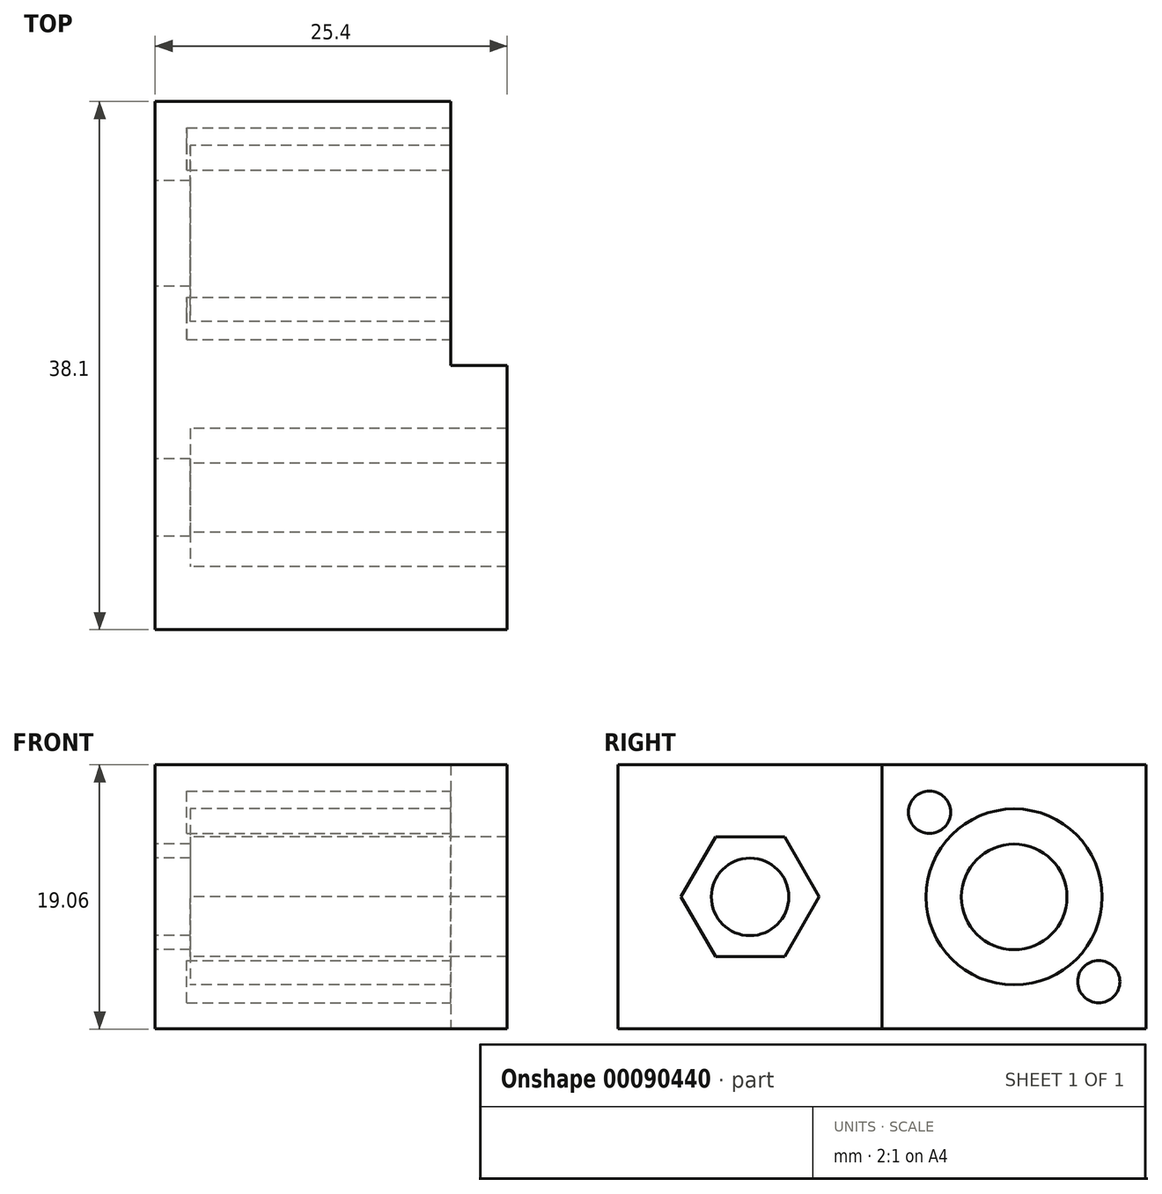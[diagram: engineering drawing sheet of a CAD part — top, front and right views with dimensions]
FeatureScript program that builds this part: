
annotation { "Feature Type Name" : "Feature", "Feature Type Description" : "" }
export const myFeature = defineFeature(function(context is Context, id is Id, definition is map)
    precondition{}
    {
        {
            var Q0;
            Q0=qCreatedBy(makeId("Right.planeOp"),FACE);
            var sketch = newSketch(context, id + "F0", { "sketchPlane" : qUnion([Q0])});
            skLineSegment(sketch, "E0", {"start": v(0, 0) * mm, "end": v(9.53, 0) * mm, "construction": true});
            skLineSegment(sketch, "E1", {"start": v(0, 0) * mm, "end": v(-9.53, 0) * mm, "construction": true});
            skLineSegment(sketch, "E2.bottom", {"start": v(-19.05, 9.53) * mm, "end": v(19.05, 9.52) * mm});
            skLineSegment(sketch, "E2.top", {"start": v(-19.05, -9.52) * mm, "end": v(19.05, -9.52) * mm});
            skLineSegment(sketch, "E2.left", {"start": v(-19.05, 9.53) * mm, "end": v(-19.05, -9.52) * mm});
            skLineSegment(sketch, "E2.right", {"start": v(19.05, 9.52) * mm, "end": v(19.05, -9.53) * mm});
            skPoint(sketch, "E2.middle", {"position": v(0, 0) * mm});
            skCircle(sketch, "E3.cCircle", {"center": v(-9.53, 0) * mm, "radius": 4.32 * mm, "construction": true});
            skLineSegment(sketch, "E3.0", {"start": v(-12.02, 4.32) * mm, "end": v(-7.03, 4.32) * mm});
            skLineSegment(sketch, "E3.1", {"start": v(-7.03, 4.32) * mm, "end": v(-4.54, 0) * mm});
            skLineSegment(sketch, "E3.2", {"start": v(-4.54, 0) * mm, "end": v(-7.03, -4.32) * mm});
            skLineSegment(sketch, "E3.3", {"start": v(-7.03, -4.32) * mm, "end": v(-12.02, -4.32) * mm});
            skLineSegment(sketch, "E3.4", {"start": v(-12.02, -4.32) * mm, "end": v(-14.51, 0) * mm});
            skLineSegment(sketch, "E3.5", {"start": v(-14.51, 0) * mm, "end": v(-12.02, 4.32) * mm});
            skPoint(sketch, "E3.0.midPoint", {"position": v(-9.53, 4.32) * mm});
            skCircle(sketch, "E4", {"center": v(9.53, 0) * mm, "radius": 6.35 * mm});
            skSolve(sketch);
        }
        {
            var Q0;
            Q0=makeQuery(id+"F0.imprint","IMPRINT",FACE,{"disambiguationData":[TD([[makeQuery(id+"F0.imprint","IMPRINT",EDGE,{"derivedFrom":sQuery(id+"F0.wireOp",EDGE,"E2.bottom")}),-1.0]])]});
            extrude(context, id + "F1", {"entities" : qUnion([Q0]), "depth" : 25.4 * mm});
        }
        {
            var Q0;
            Q0=makeQuery(id+"F1.opExtrude","CAP_FACE",FACE,{"disambiguationData":[OSD([sQuery(id+"F0.wireOp",EDGE,"E2.bottom"),sQuery(id+"F0.wireOp",EDGE,"E2.top"),sQuery(id+"F0.wireOp",EDGE,"E2.left"),sQuery(id+"F0.wireOp",EDGE,"E2.right"),sQuery(id+"F0.wireOp",EDGE,"E3.0"),sQuery(id+"F0.wireOp",EDGE,"E3.1"),sQuery(id+"F0.wireOp",EDGE,"E3.2"),sQuery(id+"F0.wireOp",EDGE,"E3.3"),sQuery(id+"F0.wireOp",EDGE,"E3.4"),sQuery(id+"F0.wireOp",EDGE,"E3.5"),sQuery(id+"F0.wireOp",EDGE,"E4")])],"isStart":true});
            var sketch = newSketch(context, id + "F2", { "sketchPlane" : qUnion([Q0])});
            skCircle(sketch, "E5", {"center": v(-9.53, 0) * mm, "radius": 3.81 * mm});
            skCircle(sketch, "E6", {"center": v(9.52, 0) * mm, "radius": 2.8 * mm});
            skLineSegment(sketch, "E7", {"start": v(12.02, 4.32) * mm, "end": v(7.03, -4.32) * mm, "construction": true});
            skLineSegment(sketch, "E8.bottom", {"start": v(-19.05, 9.52) * mm, "end": v(19.05, 9.52) * mm});
            skLineSegment(sketch, "E8.top", {"start": v(-19.05, -9.52) * mm, "end": v(19.05, -9.52) * mm});
            skLineSegment(sketch, "E8.left", {"start": v(-19.05, 9.52) * mm, "end": v(-19.05, -9.52) * mm});
            skLineSegment(sketch, "E8.right", {"start": v(19.05, 9.52) * mm, "end": v(19.05, -9.52) * mm});
            skSolve(sketch);
        }
        {
            var Q0;
            Q0 = qSketchRegion(id + "F2", true);
            extrude(context, id + "F3", {"entities" : qUnion([Q0]), "operationType" : NewBodyOperationType.ADD, "oppositeDirection" : true, "depth" : 2.54 * mm});
        }
        {
            var Q0;
            Q0=makeQuery(id+"F1.opExtrude","CAP_FACE",FACE,{"disambiguationData":[OSD([sQuery(id+"F0.wireOp",EDGE,"E2.bottom"),sQuery(id+"F0.wireOp",EDGE,"E2.top"),sQuery(id+"F0.wireOp",EDGE,"E2.left"),sQuery(id+"F0.wireOp",EDGE,"E2.right"),sQuery(id+"F0.wireOp",EDGE,"E3.0"),sQuery(id+"F0.wireOp",EDGE,"E3.1"),sQuery(id+"F0.wireOp",EDGE,"E3.2"),sQuery(id+"F0.wireOp",EDGE,"E3.3"),sQuery(id+"F0.wireOp",EDGE,"E3.4"),sQuery(id+"F0.wireOp",EDGE,"E3.5"),sQuery(id+"F0.wireOp",EDGE,"E4")])],"isStart":false});
            var sketch = newSketch(context, id + "F4", { "sketchPlane" : qUnion([Q0])});
            skLineSegment(sketch, "E9.bottom", {"start": v(19.05, 9.52) * mm, "end": v(0, 9.52) * mm});
            skLineSegment(sketch, "E9.top", {"start": v(19.05, -9.52) * mm, "end": v(0, -9.52) * mm});
            skLineSegment(sketch, "E9.left", {"start": v(19.05, 9.52) * mm, "end": v(19.05, -9.52) * mm});
            skLineSegment(sketch, "E9.right", {"start": v(0, 9.52) * mm, "end": v(0, -9.52) * mm});
            skSolve(sketch);
        }
        {
            var Q0;
            Q0 = qSketchRegion(id + "F4", true);
            extrude(context, id + "F5", {"entities" : qUnion([Q0]), "operationType" : NewBodyOperationType.REMOVE, "oppositeDirection" : true, "depth" : 4.06 * mm});
        }
        {
            var Q0;
            Q0=makeQuery(id+"F5.boolean.opBoolean","COPY",FACE,{"derivedFrom":makeQuery(id+"F5.opExtrude","CAP_FACE",FACE,{"disambiguationData":[OSD([sQuery(id+"F4.wireOp",EDGE,"E9.bottom"),sQuery(id+"F4.wireOp",EDGE,"E9.top"),sQuery(id+"F4.wireOp",EDGE,"E9.left"),sQuery(id+"F4.wireOp",EDGE,"E9.right")])],"isStart":false})});
            var sketch = newSketch(context, id + "F6", { "sketchPlane" : qUnion([Q0])});
            skLineSegment(sketch, "E10", {"start": v(9.52, 0) * mm, "end": v(3.42, 6.1) * mm, "construction": true});
            skLineSegment(sketch, "E11", {"start": v(3.42, 6.1) * mm, "end": v(0, 9.52) * mm, "construction": true});
            skLineSegment(sketch, "E12", {"start": v(9.52, 0) * mm, "end": v(15.63, -6.1) * mm, "construction": true});
            skLineSegment(sketch, "E13", {"start": v(15.63, -6.1) * mm, "end": v(19.05, -9.53) * mm, "construction": true});
            skLineSegment(sketch, "E14", {"start": v(5.03, 4.5) * mm, "end": v(3.42, 6.1) * mm, "construction": true});
            skCircle(sketch, "E15", {"center": v(3.42, 6.1) * mm, "radius": 1.52 * mm});
            skCircle(sketch, "E16", {"center": v(15.63, -6.1) * mm, "radius": 1.52 * mm});
            skSolve(sketch);
        }
        {
            var Q0;
            Q0 = qSketchRegion(id + "F6", true);
            extrude(context, id + "F7", {"entities" : qUnion([Q0]), "operationType" : NewBodyOperationType.REMOVE, "oppositeDirection" : true, "depth" : 19.05 * mm});
        }
    });
